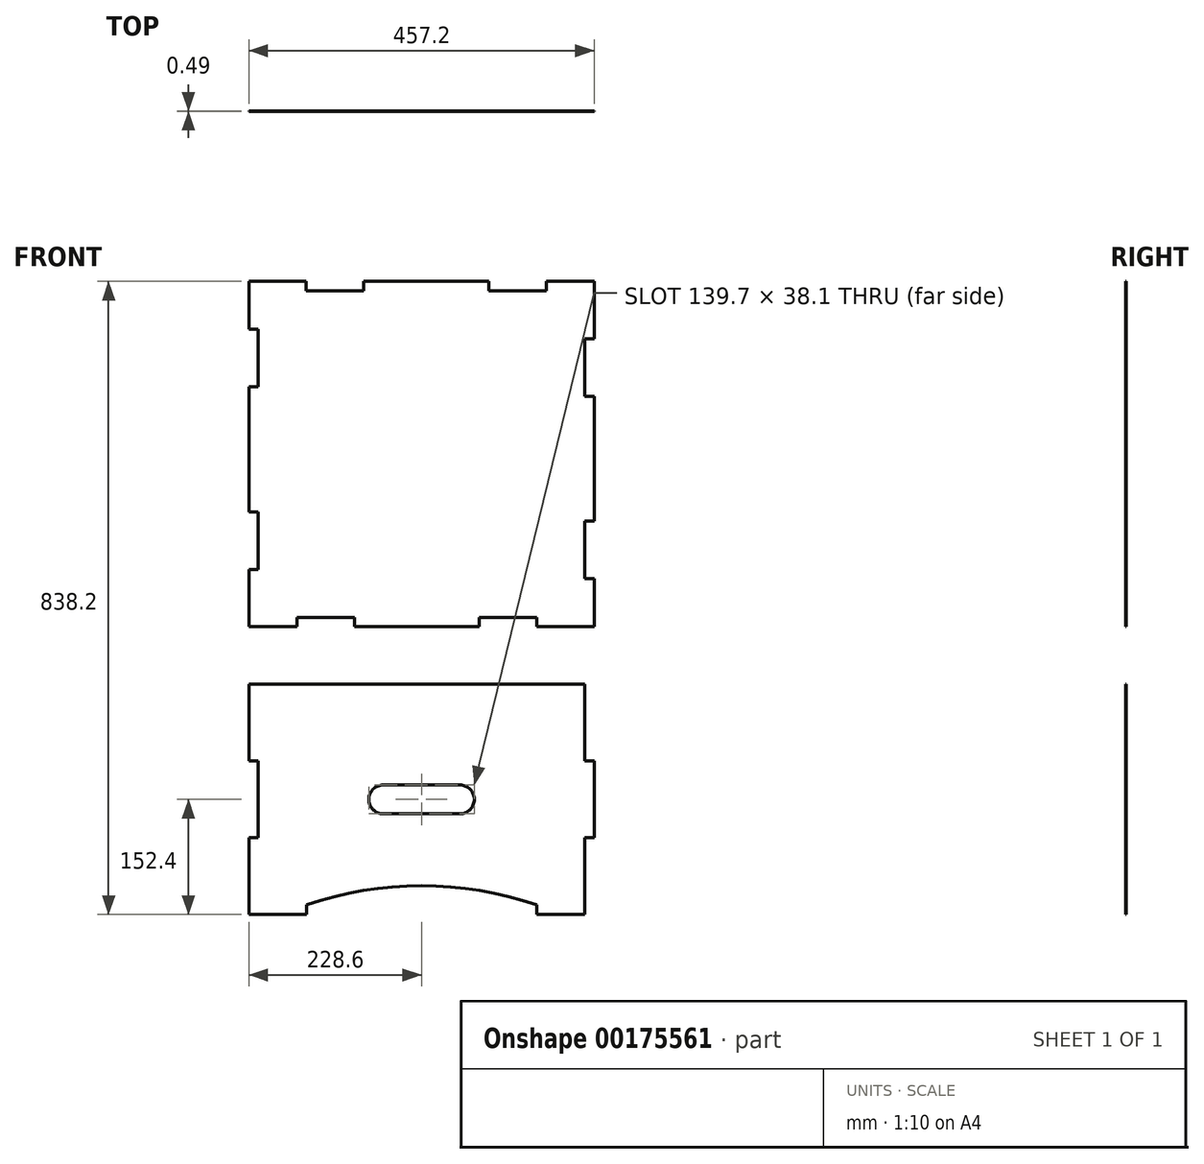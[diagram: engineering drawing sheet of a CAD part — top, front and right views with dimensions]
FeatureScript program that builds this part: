
annotation { "Feature Type Name" : "Feature", "Feature Type Description" : "" }
export const myFeature = defineFeature(function(context is Context, id is Id, definition is map)
    precondition{}
    {
        {
            assignVariable(context, id + "F0", {"name" : "ply34", "anyValue" : 0.48});
        }
        {
            var Q0;
            Q0=qCreatedBy(makeId("Front.planeOp"),FACE);
            var sketch = newSketch(context, id + "F1", { "sketchPlane" : qUnion([Q0])});
            skLineSegment(sketch, "E0.bottom", {"start": v(-222.44, 152.4) * mm, "end": v(222.44, 152.4) * mm});
            skLineSegment(sketch, "E0.top", {"start": v(-222.44, -152.4) * mm, "end": v(222.44, -152.4) * mm});
            skLineSegment(sketch, "E0.left", {"start": v(-222.44, 152.4) * mm, "end": v(-222.44, -152.4) * mm});
            skLineSegment(sketch, "E0.right", {"start": v(222.44, 152.4) * mm, "end": v(222.44, -152.4) * mm});
            skPoint(sketch, "E0.middle", {"position": v(0, 0) * mm});
            skLineSegment(sketch, "E1.bottom", {"start": v(-146.24, -152.4) * mm, "end": v(158.56, -152.4) * mm, "construction": true});
            skLineSegment(sketch, "E1.top", {"start": v(-146.24, -139.7) * mm, "end": v(158.56, -139.7) * mm, "construction": true});
            skLineSegment(sketch, "E1.left", {"start": v(-146.24, -152.4) * mm, "end": v(-146.24, -139.7) * mm});
            skLineSegment(sketch, "E1.right", {"start": v(158.56, -152.4) * mm, "end": v(158.56, -139.7) * mm});
            skLineSegment(sketch, "E2.bottom", {"start": v(222.44, 50.8) * mm, "end": v(234.76, 50.8) * mm});
            skLineSegment(sketch, "E2.top", {"start": v(222.44, -50.8) * mm, "end": v(234.76, -50.8) * mm});
            skLineSegment(sketch, "E2.left", {"start": v(222.44, 50.8) * mm, "end": v(222.44, -50.8) * mm});
            skLineSegment(sketch, "E2.right", {"start": v(234.76, 50.8) * mm, "end": v(234.76, -50.8) * mm});
            skPoint(sketch, "E3.oppositeSnap0", {"position": v(228.6, -50.8) * mm});
            skLineSegment(sketch, "E3.bottom", {"start": v(-222.44, 50.8) * mm, "end": v(-210.12, 50.8) * mm});
            skLineSegment(sketch, "E3.top", {"start": v(-222.44, -50.8) * mm, "end": v(-210.12, -50.8) * mm});
            skLineSegment(sketch, "E3.left", {"start": v(-222.44, 50.8) * mm, "end": v(-222.44, -50.8) * mm});
            skLineSegment(sketch, "E3.right", {"start": v(-210.12, 50.8) * mm, "end": v(-210.12, -50.8) * mm});
            skLineSegment(sketch, "E4", {"start": v(-44.64, 0) * mm, "end": v(56.96, 0) * mm});
            skArc(sketch, "E5.0.startCap", {"start": v(-44.64, -19.05) * mm, "mid": v(-63.7, 0) * mm, "end": v(-44.64, 19.05) * mm});
            skArc(sketch, "E5.0.endCap", {"start": v(56.96, 19.05) * mm, "mid": v(76, 0) * mm, "end": v(56.96, -19.05) * mm});
            skLineSegment(sketch, "E5.0.left", {"start": v(-44.64, 19.05) * mm, "end": v(56.96, 19.05) * mm});
            skLineSegment(sketch, "E5.0.right", {"start": v(-44.64, -19.05) * mm, "end": v(56.96, -19.05) * mm});
            skArc(sketch, "E6", {"start": v(158.56, -139.7) * mm, "mid": v(6.16, -114.3) * mm, "end": v(-146.24, -139.7) * mm});
            skLineSegment(sketch, "E7.bottom", {"start": v(-158.94, 152.4) * mm, "end": v(-82.74, 152.4) * mm});
            skLineSegment(sketch, "E7.top", {"start": v(-158.94, 164.72) * mm, "end": v(-82.74, 164.72) * mm});
            skLineSegment(sketch, "E7.left", {"start": v(-158.94, 152.4) * mm, "end": v(-158.94, 164.72) * mm});
            skLineSegment(sketch, "E7.right", {"start": v(-82.74, 152.4) * mm, "end": v(-82.74, 164.72) * mm});
            skLineSegment(sketch, "E8.bottom", {"start": v(82.74, 152.4) * mm, "end": v(158.94, 152.4) * mm});
            skLineSegment(sketch, "E8.top", {"start": v(82.74, 164.72) * mm, "end": v(158.94, 164.72) * mm});
            skLineSegment(sketch, "E8.left", {"start": v(82.74, 152.4) * mm, "end": v(82.74, 164.72) * mm});
            skLineSegment(sketch, "E8.right", {"start": v(158.94, 152.4) * mm, "end": v(158.94, 164.72) * mm});
            skLineSegment(sketch, "E9.bottom", {"start": v(-222.44, 228.6) * mm, "end": v(234.76, 228.6) * mm});
            skLineSegment(sketch, "E9.top", {"start": v(-222.44, 685.8) * mm, "end": v(234.76, 685.8) * mm});
            skLineSegment(sketch, "E9.left", {"start": v(-222.44, 228.6) * mm, "end": v(-222.44, 685.8) * mm});
            skLineSegment(sketch, "E9.right", {"start": v(234.76, 228.6) * mm, "end": v(234.76, 685.8) * mm});
            skLineSegment(sketch, "E10.bottom", {"start": v(-158.94, 228.6) * mm, "end": v(-82.74, 228.6) * mm});
            skLineSegment(sketch, "E10.top", {"start": v(-158.94, 240.92) * mm, "end": v(-82.74, 240.92) * mm});
            skLineSegment(sketch, "E10.left", {"start": v(-158.94, 228.6) * mm, "end": v(-158.94, 240.92) * mm});
            skLineSegment(sketch, "E10.right", {"start": v(-82.74, 228.6) * mm, "end": v(-82.74, 240.92) * mm});
            skLineSegment(sketch, "E11.bottom", {"start": v(82.74, 228.6) * mm, "end": v(158.94, 228.6) * mm});
            skLineSegment(sketch, "E11.top", {"start": v(82.74, 240.92) * mm, "end": v(158.94, 240.92) * mm});
            skLineSegment(sketch, "E11.left", {"start": v(82.74, 228.6) * mm, "end": v(82.74, 240.92) * mm});
            skLineSegment(sketch, "E11.right", {"start": v(158.94, 228.6) * mm, "end": v(158.94, 240.92) * mm});
            skLineSegment(sketch, "E12.bottom", {"start": v(234.76, 292.1) * mm, "end": v(222.44, 292.1) * mm});
            skLineSegment(sketch, "E12.top", {"start": v(234.76, 368.3) * mm, "end": v(222.44, 368.3) * mm});
            skLineSegment(sketch, "E12.left", {"start": v(234.76, 292.1) * mm, "end": v(234.76, 368.3) * mm});
            skLineSegment(sketch, "E12.right", {"start": v(222.44, 292.1) * mm, "end": v(222.44, 368.3) * mm});
            skLineSegment(sketch, "E13.bottom", {"start": v(234.76, 609.98) * mm, "end": v(222.44, 609.98) * mm});
            skLineSegment(sketch, "E13.top", {"start": v(234.76, 533.78) * mm, "end": v(222.44, 533.78) * mm});
            skLineSegment(sketch, "E13.left", {"start": v(234.76, 609.98) * mm, "end": v(234.76, 533.78) * mm});
            skLineSegment(sketch, "E13.right", {"start": v(222.44, 609.98) * mm, "end": v(222.44, 533.78) * mm});
            skLineSegment(sketch, "E14.bottom", {"start": v(171.26, 685.8) * mm, "end": v(95.06, 685.8) * mm});
            skLineSegment(sketch, "E14.top", {"start": v(171.26, 673.48) * mm, "end": v(95.06, 673.48) * mm});
            skLineSegment(sketch, "E14.left", {"start": v(171.26, 685.8) * mm, "end": v(171.26, 673.48) * mm});
            skLineSegment(sketch, "E14.right", {"start": v(95.06, 685.8) * mm, "end": v(95.06, 673.48) * mm});
            skLineSegment(sketch, "E15.bottom", {"start": v(-146.62, 685.8) * mm, "end": v(-70.42, 685.8) * mm});
            skLineSegment(sketch, "E15.top", {"start": v(-146.62, 673.48) * mm, "end": v(-70.42, 673.48) * mm});
            skLineSegment(sketch, "E15.left", {"start": v(-146.62, 685.8) * mm, "end": v(-146.62, 673.48) * mm});
            skLineSegment(sketch, "E15.right", {"start": v(-70.42, 685.8) * mm, "end": v(-70.42, 673.48) * mm});
            skLineSegment(sketch, "E16.bottom", {"start": v(-222.44, 304.42) * mm, "end": v(-210.12, 304.42) * mm});
            skLineSegment(sketch, "E16.top", {"start": v(-222.44, 380.62) * mm, "end": v(-210.12, 380.62) * mm});
            skLineSegment(sketch, "E16.left", {"start": v(-222.44, 304.42) * mm, "end": v(-222.44, 380.62) * mm});
            skLineSegment(sketch, "E16.right", {"start": v(-210.12, 304.42) * mm, "end": v(-210.12, 380.62) * mm});
            skLineSegment(sketch, "E17.bottom", {"start": v(-222.44, 622.3) * mm, "end": v(-210.12, 622.3) * mm});
            skLineSegment(sketch, "E17.top", {"start": v(-222.44, 546.1) * mm, "end": v(-210.12, 546.1) * mm});
            skLineSegment(sketch, "E17.left", {"start": v(-222.44, 622.3) * mm, "end": v(-222.44, 546.1) * mm});
            skLineSegment(sketch, "E17.right", {"start": v(-210.12, 622.3) * mm, "end": v(-210.12, 546.1) * mm});
            skLineSegment(sketch, "E18", {"start": v(6.16, 50.8) * mm, "end": v(6.16, 0) * mm, "construction": true});
            skLineSegment(sketch, "E19", {"start": v(-210.12, 50.8) * mm, "end": v(222.44, 50.8) * mm, "construction": true});
            skSolve(sketch);
        }
        {
            var Q0;
            Q0=makeQuery(id+"F1.imprint","IMPRINT",FACE,{"disambiguationData":[TD([[makeQuery(id+"F1.imprint","IMPRINT",EDGE,{"derivedFrom":sQuery(id+"F1.wireOp",EDGE,"kCc1j6ts-heYF-Fn3p-T1Or-9dhK8fWiCS55.bottom")}),1.0]])]});
            var Q1;
            {var subQ14=sQuery(id+"F1.wireOp",EDGE,"E1.left");Q1=makeQuery(id+"F1.imprint","IMPRINT",FACE,{"disambiguationData":[TD([[makeQuery(id+"F1.imprint","IMPRINT",EDGE,{"derivedFrom":subQ14}),1.0]])]});}
            var Q2;
            Q2=makeQuery(id+"F1.imprint","IMPRINT",FACE,{"disambiguationData":[TD([[makeQuery(id+"F1.imprint","IMPRINT",EDGE,{"derivedFrom":sQuery(id+"F1.wireOp",EDGE,"jVbOSFHp-gFmB-nsM2-l99k-Lf8UrlLDHhPC.bottom")}),-1.0]])]});
            var Q3;
            Q3=makeQuery(id+"F1.imprint","IMPRINT",FACE,{"disambiguationData":[TD([[makeQuery(id+"F1.imprint","IMPRINT",EDGE,{"derivedFrom":sQuery(id+"F1.wireOp",EDGE,"E2.bottom")}),-1.0]])]});
            var Q4;
            Q4=makeQuery(id+"F1.imprint","IMPRINT",FACE,{"disambiguationData":[TD([[makeQuery(id+"F1.imprint","IMPRINT",EDGE,{"derivedFrom":sQuery(id+"F1.wireOp",EDGE,"E7.bottom")}),1.0]])]});
            var Q5;
            Q5=makeQuery(id+"F1.imprint","IMPRINT",FACE,{"disambiguationData":[TD([[makeQuery(id+"F1.imprint","IMPRINT",EDGE,{"derivedFrom":sQuery(id+"F1.wireOp",EDGE,"E8.bottom")}),1.0]])]});
            var Q6;
            Q6=makeQuery(id+"F1.imprint","IMPRINT",FACE,{"disambiguationData":[TD([[makeQuery(id+"F1.imprint","IMPRINT",EDGE,{"derivedFrom":sQuery(id+"F1.wireOp",EDGE,"E10.top")}),1.0]])]});
            extrude(context, id + "F2", {"entities" : qUnion([Q0, Q1, Q2, Q3, Q4, Q5, Q6]), "depth" : (getVariable(context, 'ply34')) * mm});
        }
    });
